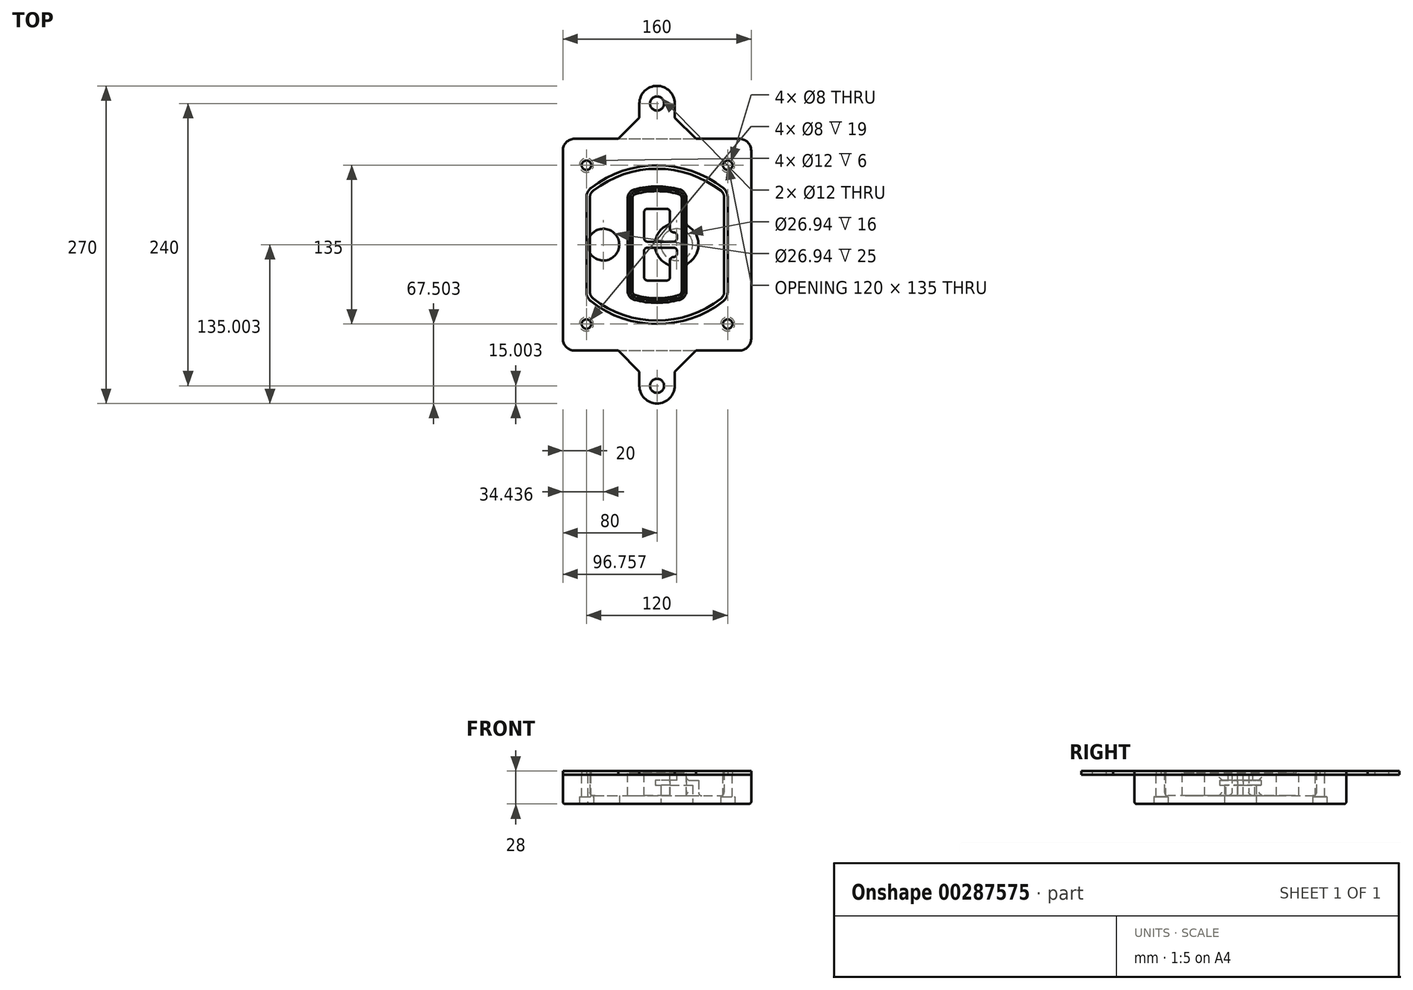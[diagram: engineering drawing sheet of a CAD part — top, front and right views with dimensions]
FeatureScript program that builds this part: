
annotation { "Feature Type Name" : "Feature", "Feature Type Description" : "" }
export const myFeature = defineFeature(function(context is Context, id is Id, definition is map)
    precondition{}
    {
        {
            var Q0;
            Q0=qCreatedBy(makeId("Top.planeOp"),FACE);
            var sketch = newSketch(context, id + "F0", { "sketchPlane" : qUnion([Q0])});
            skPoint(sketch, "E0.rect.middle", {"position": v(0, 0) * mm});
            skLineSegment(sketch, "E1.bottom", {"start": v(24.05, 28.38) * mm, "end": v(164.05, 28.38) * mm});
            skLineSegment(sketch, "E1.top", {"start": v(24.05, 208.38) * mm, "end": v(164.05, 208.38) * mm});
            skLineSegment(sketch, "E1.left", {"start": v(14.05, 38.38) * mm, "end": v(14.05, 198.38) * mm});
            skLineSegment(sketch, "E1.right", {"start": v(174.05, 38.38) * mm, "end": v(174.05, 198.38) * mm});
            skLineSegment(sketch, "E2", {"start": v(14.05, 208.38) * mm, "end": v(174.05, 28.38) * mm, "construction": true});
            skLineSegment(sketch, "E3", {"start": v(174.05, 208.38) * mm, "end": v(14.05, 28.38) * mm, "construction": true});
            skCircle(sketch, "E4", {"center": v(34.05, 185.88) * mm, "radius": 4 * mm});
            skCircle(sketch, "E5", {"center": v(154.05, 185.88) * mm, "radius": 4 * mm});
            skCircle(sketch, "E6", {"center": v(154.05, 50.88) * mm, "radius": 4 * mm});
            skCircle(sketch, "E7", {"center": v(34.05, 50.88) * mm, "radius": 4 * mm});
            skLineSegment(sketch, "E8", {"start": v(34.05, 185.88) * mm, "end": v(154.05, 185.88) * mm, "construction": true});
            skLineSegment(sketch, "E9", {"start": v(154.05, 185.88) * mm, "end": v(154.05, 50.88) * mm, "construction": true});
            skLineSegment(sketch, "E10", {"start": v(154.05, 50.88) * mm, "end": v(34.05, 50.88) * mm, "construction": true});
            skLineSegment(sketch, "E11", {"start": v(34.05, 50.88) * mm, "end": v(34.05, 185.88) * mm, "construction": true});
            skLineSegment(sketch, "E12", {"start": v(34.05, 158.68) * mm, "end": v(34.05, 78.09) * mm});
            skLineSegment(sketch, "E13", {"start": v(154.05, 158.68) * mm, "end": v(154.05, 78.09) * mm});
            skArc(sketch, "E14", {"start": v(150.2, 166.56) * mm, "mid": v(94.05, 185.88) * mm, "end": v(37.9, 166.56) * mm});
            skArc(sketch, "E15", {"start": v(37.9, 70.2) * mm, "mid": v(94.05, 50.88) * mm, "end": v(150.2, 70.2) * mm});
            skLineSegment(sketch, "E16", {"start": v(34.05, 118.38) * mm, "end": v(154.05, 118.38) * mm, "construction": true});
            skPoint(sketch, "E17.visualSharp", {"position": v(34.05, 73.38) * mm});
            skArc(sketch, "E17.filletArc", {"start": v(34.05, 78.09) * mm, "mid": v(35.06, 73.7) * mm, "end": v(37.9, 70.2) * mm});
            skPoint(sketch, "E18.visualSharp", {"position": v(34.05, 163.38) * mm});
            skArc(sketch, "E18.filletArc", {"start": v(37.9, 166.56) * mm, "mid": v(35.06, 163.06) * mm, "end": v(34.05, 158.68) * mm});
            skPoint(sketch, "E19.visualSharp", {"position": v(154.05, 163.38) * mm});
            skArc(sketch, "E19.filletArc", {"start": v(154.05, 158.68) * mm, "mid": v(153.04, 163.06) * mm, "end": v(150.2, 166.56) * mm});
            skPoint(sketch, "E20.visualSharp", {"position": v(154.05, 73.38) * mm});
            skArc(sketch, "E20.filletArc", {"start": v(150.2, 70.2) * mm, "mid": v(153.04, 73.7) * mm, "end": v(154.05, 78.09) * mm});
            skPoint(sketch, "E21.visualSharp", {"position": v(14.05, 208.38) * mm});
            skArc(sketch, "E21.filletArc", {"start": v(24.05, 208.38) * mm, "mid": v(16.98, 205.45) * mm, "end": v(14.05, 198.38) * mm});
            skPoint(sketch, "E22.visualSharp", {"position": v(174.05, 208.38) * mm});
            skArc(sketch, "E22.filletArc", {"start": v(174.05, 198.38) * mm, "mid": v(171.12, 205.45) * mm, "end": v(164.05, 208.38) * mm});
            skPoint(sketch, "E23.visualSharp", {"position": v(174.05, 28.38) * mm});
            skArc(sketch, "E23.filletArc", {"start": v(164.05, 28.38) * mm, "mid": v(171.12, 31.31) * mm, "end": v(174.05, 38.38) * mm});
            skPoint(sketch, "E24.visualSharp", {"position": v(14.05, 28.38) * mm});
            skArc(sketch, "E24.filletArc", {"start": v(14.05, 38.38) * mm, "mid": v(16.98, 31.31) * mm, "end": v(24.05, 28.38) * mm});
            skArc(sketch, "E25.0", {"start": v(151.05, 158.68) * mm, "mid": v(150.34, 161.75) * mm, "end": v(148.36, 164.2) * mm});
            skLineSegment(sketch, "E25.1", {"start": v(151.05, 158.68) * mm, "end": v(151.05, 78.09) * mm});
            skArc(sketch, "E25.2", {"start": v(148.36, 72.57) * mm, "mid": v(150.34, 75.02) * mm, "end": v(151.05, 78.09) * mm});
            skArc(sketch, "E25.3", {"start": v(39.74, 72.57) * mm, "mid": v(94.05, 53.88) * mm, "end": v(148.36, 72.57) * mm});
            skArc(sketch, "E25.4", {"start": v(37.05, 78.09) * mm, "mid": v(37.76, 75.02) * mm, "end": v(39.74, 72.57) * mm});
            skArc(sketch, "E25.5", {"start": v(148.36, 164.2) * mm, "mid": v(94.05, 182.88) * mm, "end": v(39.74, 164.2) * mm});
            skLineSegment(sketch, "E25.6", {"start": v(37.05, 158.68) * mm, "end": v(37.05, 78.09) * mm});
            skArc(sketch, "E25.7", {"start": v(39.74, 164.2) * mm, "mid": v(37.76, 161.75) * mm, "end": v(37.05, 158.68) * mm});
            skArc(sketch, "E26.0", {"start": v(35.43, 169.71) * mm, "mid": v(31.47, 164.82) * mm, "end": v(30.05, 158.68) * mm});
            skArc(sketch, "E26.1", {"start": v(152.67, 169.71) * mm, "mid": v(94.05, 189.88) * mm, "end": v(35.43, 169.71) * mm});
            skArc(sketch, "E26.2", {"start": v(158.05, 158.68) * mm, "mid": v(156.63, 164.82) * mm, "end": v(152.67, 169.71) * mm});
            skLineSegment(sketch, "E26.3", {"start": v(158.05, 158.68) * mm, "end": v(158.05, 78.09) * mm});
            skArc(sketch, "E26.4", {"start": v(152.67, 67.05) * mm, "mid": v(156.63, 71.95) * mm, "end": v(158.05, 78.09) * mm});
            skLineSegment(sketch, "E26.5", {"start": v(30.05, 158.68) * mm, "end": v(30.05, 78.09) * mm});
            skArc(sketch, "E26.6", {"start": v(35.43, 67.05) * mm, "mid": v(94.05, 46.88) * mm, "end": v(152.67, 67.05) * mm});
            skArc(sketch, "E26.7", {"start": v(30.05, 78.09) * mm, "mid": v(31.47, 71.95) * mm, "end": v(35.43, 67.05) * mm});
            skSolve(sketch);
        }
        {
            var Q0;
            Q0=makeQuery(id+"F0.imprint","IMPRINT",FACE,{"disambiguationData":[TD([[makeQuery(id+"F0.imprint","IMPRINT",EDGE,{"derivedFrom":sQuery(id+"F0.wireOp",EDGE,"E1.bottom")}),1.0]])]});
            var Q1;
            Q1=makeQuery(id+"F0.imprint","IMPRINT",FACE,{"disambiguationData":[TD([[makeQuery(id+"F0.imprint","IMPRINT",EDGE,{"derivedFrom":sQuery(id+"F0.wireOp",EDGE,"E12")}),1.0]])]});
            var Q2;
            Q2=makeQuery(id+"F0.imprint","IMPRINT",FACE,{"disambiguationData":[TD([[makeQuery(id+"F0.imprint","IMPRINT",EDGE,{"derivedFrom":sQuery(id+"F0.wireOp",EDGE,"E25.0")}),1.0]])]});
            var Q3;
            Q3=makeQuery(id+"F0.imprint","IMPRINT",FACE,{"disambiguationData":[TD([[makeQuery(id+"F0.imprint","IMPRINT",EDGE,{"derivedFrom":sQuery(id+"F0.wireOp",EDGE,"E12")}),-1.0]])]});
            extrude(context, id + "F1", {"entities" : qUnion([Q0, Q1, Q2, Q3]), "oppositeDirection" : true, "depth" : 25 * mm});
        }
        {
            var Q0;
            Q0=makeQuery(id+"F0.imprint","IMPRINT",FACE,{"disambiguationData":[TD([[makeQuery(id+"F0.imprint","IMPRINT",EDGE,{"derivedFrom":sQuery(id+"F0.wireOp",EDGE,"E12")}),1.0]])]});
            extrude(context, id + "F2", {"entities" : qUnion([Q0]), "operationType" : NewBodyOperationType.ADD, "depth" : 3 * mm});
        }
        {
            var Q0;
            Q0=makeQuery(id+"F0.imprint","IMPRINT",FACE,{"disambiguationData":[TD([[makeQuery(id+"F0.imprint","IMPRINT",EDGE,{"derivedFrom":sQuery(id+"F0.wireOp",EDGE,"E25.0")}),1.0]])]});
            extrude(context, id + "F3", {"entities" : qUnion([Q0]), "operationType" : NewBodyOperationType.REMOVE, "oppositeDirection" : true, "depth" : 18 * mm});
        }
        {
            var Q0;
            Q0=makeQuery(id+"F2.opExtrude","CAP_FACE",FACE,{"disambiguationData":[OSD([sQuery(id+"F0.wireOp",EDGE,"E12"),sQuery(id+"F0.wireOp",EDGE,"E13"),sQuery(id+"F0.wireOp",EDGE,"E14"),sQuery(id+"F0.wireOp",EDGE,"E15"),sQuery(id+"F0.wireOp",EDGE,"E17.filletArc"),sQuery(id+"F0.wireOp",EDGE,"E18.filletArc"),sQuery(id+"F0.wireOp",EDGE,"E19.filletArc"),sQuery(id+"F0.wireOp",EDGE,"E20.filletArc"),sQuery(id+"F0.wireOp",EDGE,"E25.0"),sQuery(id+"F0.wireOp",EDGE,"E25.1"),sQuery(id+"F0.wireOp",EDGE,"E25.2"),sQuery(id+"F0.wireOp",EDGE,"E25.3"),sQuery(id+"F0.wireOp",EDGE,"E25.4"),sQuery(id+"F0.wireOp",EDGE,"E25.5"),sQuery(id+"F0.wireOp",EDGE,"E25.6"),sQuery(id+"F0.wireOp",EDGE,"E25.7")])],"isStart":false});
            var sketch = newSketch(context, id + "F4", { "sketchPlane" : qUnion([Q0])});
            skArc(sketch, "E27.0", {"start": v(74.97, 71.41) * mm, "mid": v(94.05, 68.88) * mm, "end": v(113.13, 71.41) * mm});
            skArc(sketch, "E28.0", {"start": v(113.13, 165.35) * mm, "mid": v(94.05, 167.88) * mm, "end": v(74.97, 165.35) * mm});
            skLineSegment(sketch, "E29", {"start": v(69.05, 157.63) * mm, "end": v(69.05, 79.14) * mm});
            skLineSegment(sketch, "E30", {"start": v(119.05, 157.63) * mm, "end": v(119.05, 79.14) * mm});
            skLineSegment(sketch, "E31", {"start": v(69.05, 163.48) * mm, "end": v(119.05, 163.48) * mm, "construction": true});
            skLineSegment(sketch, "E32", {"start": v(69.05, 73.28) * mm, "end": v(119.05, 73.28) * mm, "construction": true});
            skPoint(sketch, "E33.visualSharp", {"position": v(69.05, 163.48) * mm});
            skArc(sketch, "E33.filletArc", {"start": v(74.97, 165.35) * mm, "mid": v(70.7, 162.5) * mm, "end": v(69.05, 157.63) * mm});
            skPoint(sketch, "E34.visualSharp", {"position": v(119.05, 163.48) * mm});
            skArc(sketch, "E34.filletArc", {"start": v(119.05, 157.63) * mm, "mid": v(117.4, 162.5) * mm, "end": v(113.13, 165.35) * mm});
            skPoint(sketch, "E35.visualSharp", {"position": v(119.05, 73.28) * mm});
            skArc(sketch, "E35.filletArc", {"start": v(113.13, 71.41) * mm, "mid": v(117.4, 74.27) * mm, "end": v(119.05, 79.14) * mm});
            skPoint(sketch, "E36.visualSharp", {"position": v(69.05, 73.28) * mm});
            skArc(sketch, "E36.filletArc", {"start": v(69.05, 79.14) * mm, "mid": v(70.7, 74.27) * mm, "end": v(74.97, 71.41) * mm});
            skArc(sketch, "E37.0", {"start": v(148.36, 164.2) * mm, "mid": v(94.05, 182.88) * mm, "end": v(39.74, 164.2) * mm});
            skArc(sketch, "E37.1", {"start": v(39.74, 164.2) * mm, "mid": v(37.76, 161.75) * mm, "end": v(37.05, 158.68) * mm});
            skLineSegment(sketch, "E37.2", {"start": v(37.05, 158.68) * mm, "end": v(37.05, 78.09) * mm});
            skArc(sketch, "E37.3", {"start": v(37.05, 78.09) * mm, "mid": v(37.76, 75.02) * mm, "end": v(39.74, 72.57) * mm});
            skArc(sketch, "E37.4", {"start": v(39.74, 72.57) * mm, "mid": v(94.05, 53.88) * mm, "end": v(148.36, 72.57) * mm});
            skArc(sketch, "E37.5", {"start": v(148.36, 72.57) * mm, "mid": v(150.34, 75.02) * mm, "end": v(151.05, 78.09) * mm});
            skLineSegment(sketch, "E37.6", {"start": v(151.05, 158.68) * mm, "end": v(151.05, 78.09) * mm});
            skArc(sketch, "E37.7", {"start": v(151.05, 158.68) * mm, "mid": v(150.34, 161.75) * mm, "end": v(148.36, 164.2) * mm});
            skLineSegment(sketch, "E38.0", {"start": v(117.05, 157.63) * mm, "end": v(117.05, 79.14) * mm});
            skArc(sketch, "E38.1", {"start": v(112.61, 73.34) * mm, "mid": v(115.81, 75.49) * mm, "end": v(117.05, 79.14) * mm});
            skArc(sketch, "E38.2", {"start": v(75.49, 73.34) * mm, "mid": v(94.05, 70.88) * mm, "end": v(112.61, 73.34) * mm});
            skArc(sketch, "E38.3", {"start": v(71.05, 79.14) * mm, "mid": v(72.29, 75.49) * mm, "end": v(75.49, 73.34) * mm});
            skLineSegment(sketch, "E38.4", {"start": v(71.05, 157.63) * mm, "end": v(71.05, 79.14) * mm});
            skArc(sketch, "E38.5", {"start": v(117.05, 157.63) * mm, "mid": v(115.81, 161.28) * mm, "end": v(112.61, 163.42) * mm});
            skArc(sketch, "E38.6", {"start": v(75.49, 163.42) * mm, "mid": v(72.29, 161.28) * mm, "end": v(71.05, 157.63) * mm});
            skArc(sketch, "E38.7", {"start": v(112.61, 163.42) * mm, "mid": v(94.05, 165.88) * mm, "end": v(75.49, 163.42) * mm});
            skArc(sketch, "E39.0", {"start": v(115.05, 157.63) * mm, "mid": v(114.23, 160.06) * mm, "end": v(112.1, 161.5) * mm});
            skLineSegment(sketch, "E39.1", {"start": v(115.05, 157.63) * mm, "end": v(115.05, 79.14) * mm});
            skArc(sketch, "E39.2", {"start": v(112.1, 75.27) * mm, "mid": v(114.23, 76.7) * mm, "end": v(115.05, 79.14) * mm});
            skArc(sketch, "E39.3", {"start": v(76, 75.27) * mm, "mid": v(94.05, 72.88) * mm, "end": v(112.1, 75.27) * mm});
            skArc(sketch, "E39.4", {"start": v(73.05, 79.14) * mm, "mid": v(73.87, 76.7) * mm, "end": v(76, 75.27) * mm});
            skArc(sketch, "E39.5", {"start": v(112.1, 161.5) * mm, "mid": v(94.05, 163.88) * mm, "end": v(76, 161.5) * mm});
            skLineSegment(sketch, "E39.6", {"start": v(73.05, 157.63) * mm, "end": v(73.05, 79.14) * mm});
            skArc(sketch, "E39.7", {"start": v(76, 161.5) * mm, "mid": v(73.87, 160.06) * mm, "end": v(73.05, 157.63) * mm});
            skLineSegment(sketch, "E40", {"start": v(69.05, 118.38) * mm, "end": v(119.05, 118.38) * mm, "construction": true});
            skLineSegment(sketch, "E41", {"start": v(83.05, 123.88) * mm, "end": v(83.05, 145.88) * mm});
            skLineSegment(sketch, "E42", {"start": v(86.05, 148.88) * mm, "end": v(102.05, 148.88) * mm});
            skLineSegment(sketch, "E43", {"start": v(105.05, 145.88) * mm, "end": v(105.05, 131.88) * mm});
            skLineSegment(sketch, "E44", {"start": v(108.05, 128.88) * mm, "end": v(108.05, 128.88) * mm});
            skLineSegment(sketch, "E45", {"start": v(111.05, 125.88) * mm, "end": v(111.05, 123.88) * mm});
            skLineSegment(sketch, "E46", {"start": v(108.05, 120.88) * mm, "end": v(86.05, 120.88) * mm});
            skPoint(sketch, "E47.visualSharp", {"position": v(83.05, 148.88) * mm});
            skArc(sketch, "E47.filletArc", {"start": v(86.05, 148.88) * mm, "mid": v(83.93, 148) * mm, "end": v(83.05, 145.88) * mm});
            skPoint(sketch, "E48.visualSharp", {"position": v(105.05, 148.88) * mm});
            skArc(sketch, "E48.filletArc", {"start": v(105.05, 145.88) * mm, "mid": v(104.17, 148) * mm, "end": v(102.05, 148.88) * mm});
            skPoint(sketch, "E49.visualSharp", {"position": v(105.05, 128.88) * mm});
            skArc(sketch, "E49.filletArc", {"start": v(105.05, 131.88) * mm, "mid": v(105.93, 129.76) * mm, "end": v(108.05, 128.88) * mm});
            skPoint(sketch, "E50.visualSharp", {"position": v(111.05, 128.88) * mm});
            skArc(sketch, "E50.filletArc", {"start": v(111.05, 125.88) * mm, "mid": v(110.17, 128) * mm, "end": v(108.05, 128.88) * mm});
            skPoint(sketch, "E51.visualSharp", {"position": v(111.05, 120.88) * mm});
            skArc(sketch, "E51.filletArc", {"start": v(108.05, 120.88) * mm, "mid": v(110.17, 121.76) * mm, "end": v(111.05, 123.88) * mm});
            skPoint(sketch, "E52.visualSharp", {"position": v(83.05, 120.88) * mm});
            skArc(sketch, "E52.filletArc", {"start": v(83.05, 123.88) * mm, "mid": v(83.93, 121.76) * mm, "end": v(86.05, 120.88) * mm});
            skLineSegment(sketch, "E53.0.MirrorCS", {"start": v(108.05, 115.88) * mm, "end": v(86.05, 115.88) * mm});
            skArc(sketch, "E54.0.MirrorCS", {"start": v(83.05, 112.88) * mm, "mid": v(83.93, 115) * mm, "end": v(86.05, 115.88) * mm});
            skLineSegment(sketch, "E55.0.MirrorCS", {"start": v(83.05, 112.88) * mm, "end": v(83.05, 90.88) * mm});
            skArc(sketch, "E56.0.MirrorCS", {"start": v(86.05, 87.88) * mm, "mid": v(83.93, 88.76) * mm, "end": v(83.05, 90.88) * mm});
            skLineSegment(sketch, "E57.0.MirrorCS", {"start": v(86.05, 87.88) * mm, "end": v(102.05, 87.88) * mm});
            skArc(sketch, "E58.0.MirrorCS", {"start": v(105.05, 90.88) * mm, "mid": v(104.17, 88.76) * mm, "end": v(102.05, 87.88) * mm});
            skLineSegment(sketch, "E59.0.MirrorCS", {"start": v(105.05, 90.88) * mm, "end": v(105.05, 104.88) * mm});
            skArc(sketch, "E60.0.MirrorCS", {"start": v(105.05, 104.88) * mm, "mid": v(105.93, 107) * mm, "end": v(108.05, 107.88) * mm});
            skArc(sketch, "E61.0.MirrorCS", {"start": v(111.05, 110.88) * mm, "mid": v(110.17, 108.76) * mm, "end": v(108.05, 107.88) * mm});
            skLineSegment(sketch, "E62.0.MirrorCS", {"start": v(111.05, 110.88) * mm, "end": v(111.05, 112.88) * mm});
            skArc(sketch, "E63.0.MirrorCS", {"start": v(108.05, 115.88) * mm, "mid": v(110.17, 115) * mm, "end": v(111.05, 112.88) * mm});
            skSolve(sketch);
        }
        {
            var Q0;
            Q0=makeQuery(id+"F4.imprint","IMPRINT",FACE,{"disambiguationData":[TD([[makeQuery(id+"F4.imprint","IMPRINT",EDGE,{"derivedFrom":sQuery(id+"F4.wireOp",EDGE,"E27.0")}),1.0]])]});
            var Q1;
            Q1=makeQuery(id+"F4.imprint","IMPRINT",FACE,{"disambiguationData":[TD([[makeQuery(id+"F4.imprint","IMPRINT",EDGE,{"derivedFrom":sQuery(id+"F4.wireOp",EDGE,"E38.0")}),-1.0]])]});
            var Q2;
            Q2=makeQuery(id+"F4.imprint","IMPRINT",FACE,{"disambiguationData":[TD([[makeQuery(id+"F4.imprint","IMPRINT",EDGE,{"derivedFrom":sQuery(id+"F4.wireOp",EDGE,"E39.0")}),1.0]])]});
            extrude(context, id + "F5", {"entities" : qUnion([Q0, Q1, Q2]), "operationType" : NewBodyOperationType.ADD, "endBound" : BoundingType.UP_TO_NEXT, "oppositeDirection" : true, "depth" : 25 * mm});
        }
        {
            var Q0;
            Q0=makeQuery(id+"F4.imprint","IMPRINT",FACE,{"disambiguationData":[TD([[makeQuery(id+"F4.imprint","IMPRINT",EDGE,{"derivedFrom":sQuery(id+"F4.wireOp",EDGE,"E38.0")}),-1.0]])]});
            extrude(context, id + "F6", {"entities" : qUnion([Q0]), "operationType" : NewBodyOperationType.REMOVE, "oppositeDirection" : true, "depth" : 2 * mm});
        }
        {
            var Q0;
            Q0=makeQuery(id+"F1.opExtrude","CAP_FACE",FACE,{"disambiguationData":[OSD([sQuery(id+"F0.wireOp",EDGE,"E1.bottom"),sQuery(id+"F0.wireOp",EDGE,"E1.top"),sQuery(id+"F0.wireOp",EDGE,"E1.left"),sQuery(id+"F0.wireOp",EDGE,"E1.right"),sQuery(id+"F0.wireOp",EDGE,"E4"),sQuery(id+"F0.wireOp",EDGE,"E5"),sQuery(id+"F0.wireOp",EDGE,"E6"),sQuery(id+"F0.wireOp",EDGE,"E7"),sQuery(id+"F0.wireOp",EDGE,"E21.filletArc"),sQuery(id+"F0.wireOp",EDGE,"E22.filletArc"),sQuery(id+"F0.wireOp",EDGE,"E23.filletArc"),sQuery(id+"F0.wireOp",EDGE,"E24.filletArc")])],"isStart":false});
            var sketch = newSketch(context, id + "F7", { "sketchPlane" : qUnion([Q0])});
            skCircle(sketch, "E64", {"center": v(110.8, -118.38) * mm, "radius": 13.47 * mm});
            skCircle(sketch, "E65", {"center": v(48.49, -118.38) * mm, "radius": 13.47 * mm});
            skLineSegment(sketch, "E66", {"start": v(174.05, -118.38) * mm, "end": v(14.05, -118.38) * mm});
            skCircle(sketch, "E67", {"center": v(110.8, -118.38) * mm, "radius": 18.47 * mm});
            skCircle(sketch, "E68", {"center": v(154.05, -185.88) * mm, "radius": 6 * mm});
            skCircle(sketch, "E69", {"center": v(34.05, -185.88) * mm, "radius": 6 * mm});
            skCircle(sketch, "E70", {"center": v(34.05, -50.88) * mm, "radius": 6 * mm});
            skCircle(sketch, "E71", {"center": v(154.05, -50.88) * mm, "radius": 6 * mm});
            skSolve(sketch);
        }
        {
            var Q0;
            {var subQ1=sQuery(id+"F7.wireOp",EDGE,"E66");var subQ4=sQuery(id+"F7.wireOp",EDGE,"E64");var subQ6=makeQuery(id+"F7.imprint","INTERSECT",VERTEX,{"disambiguationData":[OD(0.0)],"derivedFrom":[subQ4,subQ1]});Q0=makeQuery(id+"F7.imprint","IMPRINT",FACE,{"disambiguationData":[TD([[makeQuery(id+"F7.imprint","IMPRINT",EDGE,{"disambiguationData":[TD([[subQ6,-1.0]])],"derivedFrom":subQ4}),-1.0]])]});}
            var Q1;
            {var subQ0=sQuery(id+"F7.wireOp",EDGE,"E66");var subQ1=sQuery(id+"F7.wireOp",EDGE,"E64");var subQ3=makeQuery(id+"F7.imprint","INTERSECT",VERTEX,{"disambiguationData":[OD(0.0)],"derivedFrom":[subQ1,subQ0]});Q1=makeQuery(id+"F7.imprint","IMPRINT",FACE,{"disambiguationData":[TD([[makeQuery(id+"F7.imprint","IMPRINT",EDGE,{"disambiguationData":[TD([[subQ3,-1.0]])],"derivedFrom":subQ1}),1.0]])]});}
            var Q2;
            {var subQ0=sQuery(id+"F7.wireOp",EDGE,"E66");var subQ1=sQuery(id+"F7.wireOp",EDGE,"E64");var subQ3=makeQuery(id+"F7.imprint","INTERSECT",VERTEX,{"disambiguationData":[OD(0.0)],"derivedFrom":[subQ1,subQ0]});Q2=makeQuery(id+"F7.imprint","IMPRINT",FACE,{"disambiguationData":[TD([[makeQuery(id+"F7.imprint","IMPRINT",EDGE,{"disambiguationData":[TD([[subQ3,1.0]])],"derivedFrom":subQ1}),1.0]])]});}
            var Q3;
            {var subQ1=sQuery(id+"F7.wireOp",EDGE,"E66");var subQ4=sQuery(id+"F7.wireOp",EDGE,"E64");var subQ6=makeQuery(id+"F7.imprint","INTERSECT",VERTEX,{"disambiguationData":[OD(0.0)],"derivedFrom":[subQ4,subQ1]});Q3=makeQuery(id+"F7.imprint","IMPRINT",FACE,{"disambiguationData":[TD([[makeQuery(id+"F7.imprint","IMPRINT",EDGE,{"disambiguationData":[TD([[subQ6,1.0]])],"derivedFrom":subQ4}),-1.0]])]});}
            extrude(context, id + "F8", {"entities" : qUnion([Q0, Q1, Q2, Q3]), "operationType" : NewBodyOperationType.ADD, "oppositeDirection" : true, "depth" : 20 * mm});
        }
        {
            var Q0;
            {var subQ0=sQuery(id+"F7.wireOp",EDGE,"E66");var subQ1=sQuery(id+"F7.wireOp",EDGE,"E64");var subQ3=makeQuery(id+"F7.imprint","INTERSECT",VERTEX,{"disambiguationData":[OD(0.0)],"derivedFrom":[subQ1,subQ0]});Q0=makeQuery(id+"F7.imprint","IMPRINT",FACE,{"disambiguationData":[TD([[makeQuery(id+"F7.imprint","IMPRINT",EDGE,{"disambiguationData":[TD([[subQ3,-1.0]])],"derivedFrom":subQ1}),1.0]])]});}
            var Q1;
            {var subQ0=sQuery(id+"F7.wireOp",EDGE,"E66");var subQ1=sQuery(id+"F7.wireOp",EDGE,"E64");var subQ3=makeQuery(id+"F7.imprint","INTERSECT",VERTEX,{"disambiguationData":[OD(0.0)],"derivedFrom":[subQ1,subQ0]});Q1=makeQuery(id+"F7.imprint","IMPRINT",FACE,{"disambiguationData":[TD([[makeQuery(id+"F7.imprint","IMPRINT",EDGE,{"disambiguationData":[TD([[subQ3,1.0]])],"derivedFrom":subQ1}),1.0]])]});}
            extrude(context, id + "F9", {"entities" : qUnion([Q0, Q1]), "operationType" : NewBodyOperationType.REMOVE, "oppositeDirection" : true, "depth" : 16 * mm});
        }
        {
            var Q0;
            {var subQ0=sQuery(id+"F7.wireOp",EDGE,"E66");var subQ1=sQuery(id+"F7.wireOp",EDGE,"E65");var subQ3=makeQuery(id+"F7.imprint","INTERSECT",VERTEX,{"disambiguationData":[OD(0.0)],"derivedFrom":[subQ1,subQ0]});Q0=makeQuery(id+"F7.imprint","IMPRINT",FACE,{"disambiguationData":[TD([[makeQuery(id+"F7.imprint","IMPRINT",EDGE,{"disambiguationData":[TD([[subQ3,-1.0]])],"derivedFrom":subQ1}),1.0]])]});}
            var Q1;
            {var subQ0=sQuery(id+"F7.wireOp",EDGE,"E66");var subQ1=sQuery(id+"F7.wireOp",EDGE,"E65");var subQ3=makeQuery(id+"F7.imprint","INTERSECT",VERTEX,{"disambiguationData":[OD(0.0)],"derivedFrom":[subQ1,subQ0]});Q1=makeQuery(id+"F7.imprint","IMPRINT",FACE,{"disambiguationData":[TD([[makeQuery(id+"F7.imprint","IMPRINT",EDGE,{"disambiguationData":[TD([[subQ3,1.0]])],"derivedFrom":subQ1}),1.0]])]});}
            extrude(context, id + "F10", {"entities" : qUnion([Q0, Q1]), "operationType" : NewBodyOperationType.REMOVE, "oppositeDirection" : true, "depth" : 25 * mm});
        }
        {
            var Q0;
            Q0=makeQuery(id+"F7.imprint","IMPRINT",FACE,{"disambiguationData":[TD([[makeQuery(id+"F7.imprint","IMPRINT",EDGE,{"derivedFrom":sQuery(id+"F7.wireOp",EDGE,"E68")}),1.0]])]});
            var Q1;
            Q1=makeQuery(id+"F7.imprint","IMPRINT",FACE,{"disambiguationData":[TD([[makeQuery(id+"F7.imprint","IMPRINT",EDGE,{"derivedFrom":makeQuery(id+"F1.opExtrude","CAP_EDGE",EDGE,{"disambiguationData":[OSD([sQuery(id+"F0.wireOp",EDGE,"E5")])],"isStart":false})}),-1.0]])]});
            var Q2;
            Q2=makeQuery(id+"F7.imprint","IMPRINT",FACE,{"disambiguationData":[TD([[makeQuery(id+"F7.imprint","IMPRINT",EDGE,{"derivedFrom":sQuery(id+"F7.wireOp",EDGE,"E69")}),1.0]])]});
            var Q3;
            Q3=makeQuery(id+"F7.imprint","IMPRINT",FACE,{"disambiguationData":[TD([[makeQuery(id+"F7.imprint","IMPRINT",EDGE,{"derivedFrom":makeQuery(id+"F1.opExtrude","CAP_EDGE",EDGE,{"disambiguationData":[OSD([sQuery(id+"F0.wireOp",EDGE,"E4")])],"isStart":false})}),-1.0]])]});
            var Q4;
            Q4=makeQuery(id+"F7.imprint","IMPRINT",FACE,{"disambiguationData":[TD([[makeQuery(id+"F7.imprint","IMPRINT",EDGE,{"derivedFrom":sQuery(id+"F7.wireOp",EDGE,"E70")}),1.0]])]});
            var Q5;
            Q5=makeQuery(id+"F7.imprint","IMPRINT",FACE,{"disambiguationData":[TD([[makeQuery(id+"F7.imprint","IMPRINT",EDGE,{"derivedFrom":makeQuery(id+"F1.opExtrude","CAP_EDGE",EDGE,{"disambiguationData":[OSD([sQuery(id+"F0.wireOp",EDGE,"E7")])],"isStart":false})}),-1.0]])]});
            var Q6;
            Q6=makeQuery(id+"F7.imprint","IMPRINT",FACE,{"disambiguationData":[TD([[makeQuery(id+"F7.imprint","IMPRINT",EDGE,{"derivedFrom":sQuery(id+"F7.wireOp",EDGE,"E71")}),1.0]])]});
            var Q7;
            Q7=makeQuery(id+"F7.imprint","IMPRINT",FACE,{"disambiguationData":[TD([[makeQuery(id+"F7.imprint","IMPRINT",EDGE,{"derivedFrom":makeQuery(id+"F1.opExtrude","CAP_EDGE",EDGE,{"disambiguationData":[OSD([sQuery(id+"F0.wireOp",EDGE,"E6")])],"isStart":false})}),-1.0]])]});
            extrude(context, id + "F11", {"entities" : qUnion([Q0, Q1, Q2, Q3, Q4, Q5, Q6, Q7]), "operationType" : NewBodyOperationType.REMOVE, "oppositeDirection" : true, "depth" : 6 * mm});
        }
        {
            var Q0;
            Q0=makeQuery(id+"F9.boolean.opBoolean","COPY",FACE,{"derivedFrom":makeQuery(id+"F9.opExtrude","CAP_FACE",FACE,{"disambiguationData":[OSD([sQuery(id+"F7.wireOp",EDGE,"E64")])],"isStart":false})});
            var sketch = newSketch(context, id + "F12", { "sketchPlane" : qUnion([Q0])});
            skArc(sketch, "E72.0", {"start": v(105.05, -100.83) * mm, "mid": v(96.62, -106.56) * mm, "end": v(92.5, -115.88) * mm});
            skArc(sketch, "E72.1", {"start": v(92.5, -120.88) * mm, "mid": v(96.62, -130.2) * mm, "end": v(105.05, -135.93) * mm});
            skLineSegment(sketch, "E73", {"start": v(92.5, -120.88) * mm, "end": v(108.05, -120.88) * mm});
            skLineSegment(sketch, "E74.0", {"start": v(108.05, -115.88) * mm, "end": v(92.5, -115.88) * mm});
            skArc(sketch, "E74.1", {"start": v(108.05, -115.88) * mm, "mid": v(110.17, -115) * mm, "end": v(111.05, -112.88) * mm});
            skLineSegment(sketch, "E74.2", {"start": v(111.05, -110.88) * mm, "end": v(111.05, -112.88) * mm});
            skArc(sketch, "E74.3", {"start": v(111.05, -110.88) * mm, "mid": v(110.17, -108.76) * mm, "end": v(108.05, -107.88) * mm});
            skArc(sketch, "E74.4", {"start": v(105.05, -104.88) * mm, "mid": v(105.93, -107) * mm, "end": v(108.05, -107.88) * mm});
            skLineSegment(sketch, "E74.5", {"start": v(105.05, -100.83) * mm, "end": v(105.05, -104.88) * mm});
            skLineSegment(sketch, "E74.7", {"start": v(108.05, -120.88) * mm, "end": v(92.5, -120.88) * mm});
            skArc(sketch, "E74.8", {"start": v(108.05, -120.88) * mm, "mid": v(110.17, -121.76) * mm, "end": v(111.05, -123.88) * mm});
            skLineSegment(sketch, "E74.9", {"start": v(111.05, -125.88) * mm, "end": v(111.05, -123.88) * mm});
            skArc(sketch, "E74.10", {"start": v(111.05, -125.88) * mm, "mid": v(110.17, -128) * mm, "end": v(108.05, -128.88) * mm});
            skArc(sketch, "E74.11", {"start": v(105.05, -131.88) * mm, "mid": v(105.93, -129.76) * mm, "end": v(108.05, -128.88) * mm});
            skLineSegment(sketch, "E74.12", {"start": v(105.05, -135.93) * mm, "end": v(105.05, -131.88) * mm});
            skPoint(sketch, "E75.orphan", {"position": v(105.05, -145.88) * mm});
            skPoint(sketch, "E76.orphan", {"position": v(86.05, -120.88) * mm});
            skPoint(sketch, "E77.orphan", {"position": v(86.05, -115.88) * mm});
            skPoint(sketch, "E78.orphan", {"position": v(105.05, -90.88) * mm});
            skSolve(sketch);
        }
        {
            var Q0;
            {var subQ7=sQuery(id+"F12.wireOp",EDGE,"E72.0");var subQ14=sQuery(id+"F12.wireOp",EDGE,"E72.1");var subQ16=sQuery(id+"F12.wireOp",EDGE,"E74.1");var subQ18=sQuery(id+"F12.wireOp",EDGE,"E74.8");Q0=qUnion([makeQuery(id+"F12.imprint","IMPRINT",FACE,{"disambiguationData":[TD([[makeQuery(id+"F12.imprint","IMPRINT",EDGE,{"derivedFrom":subQ7}),1.0]])]}),makeQuery(id+"F12.imprint","IMPRINT",FACE,{"disambiguationData":[TD([[makeQuery(id+"F12.imprint","IMPRINT",EDGE,{"derivedFrom":subQ14}),1.0]])]}),makeQuery(id+"F12.imprint","IMPRINT",FACE,{"disambiguationData":[TD([[makeQuery(id+"F12.imprint","IMPRINT",EDGE,{"derivedFrom":subQ16}),1.0]])]}),makeQuery(id+"F12.imprint","IMPRINT",FACE,{"disambiguationData":[TD([[makeQuery(id+"F12.imprint","IMPRINT",EDGE,{"derivedFrom":subQ18}),-1.0]])]})]);}
            var Q1;
            Q1=makeQuery(id+"F5.boolean.opBoolean","SPLIT",FACE,{"disambiguationData":[TD([makeQuery(id+"F5.opExtrude","SWEPT_FACE",FACE,{"disambiguationData":[OSD([sQuery(id+"F4.wireOp",EDGE,"E41")])]})])],"derivedFrom":makeQuery(id+"F3.boolean.opBoolean","COPY",FACE,{"derivedFrom":makeQuery(id+"F3.opExtrude","CAP_FACE",FACE,{"disambiguationData":[OSD([sQuery(id+"F0.wireOp",EDGE,"E25.0"),sQuery(id+"F0.wireOp",EDGE,"E25.1"),sQuery(id+"F0.wireOp",EDGE,"E25.2"),sQuery(id+"F0.wireOp",EDGE,"E25.3"),sQuery(id+"F0.wireOp",EDGE,"E25.4"),sQuery(id+"F0.wireOp",EDGE,"E25.5"),sQuery(id+"F0.wireOp",EDGE,"E25.6"),sQuery(id+"F0.wireOp",EDGE,"E25.7")])],"isStart":false})})});
            extrude(context, id + "F13", {"entities" : qUnion([Q0]), "operationType" : NewBodyOperationType.REMOVE, "endBound" : BoundingType.UP_TO_SURFACE, "endBoundEntityFace" : qUnion([Q1]), "depth" : 25 * mm});
        }
        {
            var Q0;
            {var subQ0=sQuery(id+"F0.wireOp",EDGE,"E25.6");var subQ1=makeQuery(id+"F3.boolean.opBoolean","COPY",EDGE,{"derivedFrom":makeQuery(id+"F3.opExtrude","CAP_EDGE",EDGE,{"disambiguationData":[OSD([subQ0])],"isStart":false})});var subQ4=sQuery(id+"F0.wireOp",EDGE,"E25.4");var subQ5=sQuery(id+"F0.wireOp",EDGE,"E25.7");Q0=qUnion([makeQuery(id+"F10.boolean.opBoolean","SPLIT",EDGE,{"disambiguationData":[TD([makeQuery(id+"F2.opExtrude","SWEPT_FACE",FACE,{"disambiguationData":[OSD([subQ4])]})])],"derivedFrom":subQ1}),makeQuery(id+"F10.boolean.opBoolean","SPLIT",EDGE,{"disambiguationData":[TD([makeQuery(id+"F2.opExtrude","SWEPT_FACE",FACE,{"disambiguationData":[OSD([subQ5])]})])],"derivedFrom":subQ1})]);}
            var Q1;
            Q1=makeQuery(id+"F8.boolean.opBoolean","INTERSECT",EDGE,{"derivedFrom":[makeQuery(id+"F5.opExtrude","SWEPT_FACE",FACE,{"disambiguationData":[OSD([sQuery(id+"F4.wireOp",EDGE,"E30")])]}),makeQuery(id+"F8.opExtrude","CAP_FACE",FACE,{"disambiguationData":[OSD([sQuery(id+"F7.wireOp",EDGE,"E67")])],"isStart":false})]});
            var Q2;
            Q2=makeQuery(id+"F8.boolean.opBoolean","INTERSECT",EDGE,{"disambiguationData":[OD(1.0)],"derivedFrom":[makeQuery(id+"F5.opExtrude","SWEPT_FACE",FACE,{"disambiguationData":[OSD([sQuery(id+"F4.wireOp",EDGE,"E30")])]}),makeQuery(id+"F8.opExtrude","SWEPT_FACE",FACE,{"disambiguationData":[OSD([sQuery(id+"F7.wireOp",EDGE,"E67")])]})]});
            var Q3;
            {var subQ0=sQuery(id+"F4.wireOp",EDGE,"E30");Q3=makeQuery(id+"F8.boolean.opBoolean","SPLIT",EDGE,{"disambiguationData":[TD([makeQuery(id+"F5.opExtrude","SWEPT_FACE",FACE,{"disambiguationData":[OSD([sQuery(id+"F4.wireOp",EDGE,"E35.filletArc")])]})])],"derivedFrom":makeQuery(id+"F5.opExtrude","CAP_EDGE",EDGE,{"disambiguationData":[OSD([subQ0])],"isStart":false})});}
            var Q4;
            {var subQ0=sQuery(id+"F0.wireOp",EDGE,"E25.7");var subQ1=sQuery(id+"F0.wireOp",EDGE,"E25.1");var subQ2=sQuery(id+"F0.wireOp",EDGE,"E25.6");var subQ3=sQuery(id+"F0.wireOp",EDGE,"E25.5");var subQ4=sQuery(id+"F0.wireOp",EDGE,"E25.4");var subQ5=sQuery(id+"F0.wireOp",EDGE,"E25.0");var subQ6=sQuery(id+"F0.wireOp",EDGE,"E25.2");var subQ7=sQuery(id+"F0.wireOp",EDGE,"E25.3");Q4=makeQuery(id+"F8.boolean.opBoolean","INTERSECT",EDGE,{"derivedFrom":[makeQuery(id+"F5.boolean.opBoolean","SPLIT",FACE,{"disambiguationData":[TD([makeQuery(id+"F2.opExtrude","SWEPT_FACE",FACE,{"disambiguationData":[OSD([subQ5])]})])],"derivedFrom":makeQuery(id+"F3.boolean.opBoolean","COPY",FACE,{"derivedFrom":makeQuery(id+"F3.opExtrude","CAP_FACE",FACE,{"disambiguationData":[OSD([subQ5,subQ1,subQ6,subQ7,subQ4,subQ3,subQ2,subQ0])],"isStart":false})})}),makeQuery(id+"F8.opExtrude","SWEPT_FACE",FACE,{"disambiguationData":[OSD([sQuery(id+"F7.wireOp",EDGE,"E67")])]})]});}
            var Q5;
            Q5=makeQuery(id+"F8.boolean.opBoolean","INTERSECT",EDGE,{"disambiguationData":[OD(0.0)],"derivedFrom":[makeQuery(id+"F5.opExtrude","SWEPT_FACE",FACE,{"disambiguationData":[OSD([sQuery(id+"F4.wireOp",EDGE,"E30")])]}),makeQuery(id+"F8.opExtrude","SWEPT_FACE",FACE,{"disambiguationData":[OSD([sQuery(id+"F7.wireOp",EDGE,"E67")])]})]});
            fillet(context, id + "F14", {"entities" : qUnion([Q0, Q1, Q2, Q3, Q4, Q5]), "radius" : 3 * mm, "tangentPropagation" : true, "allowEdgeOverflow" : false});
        }
        {
            var Q0;
            Q0=makeQuery(id+"F1.opExtrude","CAP_EDGE",EDGE,{"disambiguationData":[OSD([sQuery(id+"F0.wireOp",EDGE,"E1.bottom")])],"isStart":false});
            fillet(context, id + "F15", {"entities" : qUnion([Q0]), "radius" : 2 * mm, "tangentPropagation" : true, "allowEdgeOverflow" : false});
        }
        {
            var Q0;
            {var subQ0=sQuery(id+"F0.wireOp",EDGE,"E1.bottom");var subQ1=sQuery(id+"F0.wireOp",EDGE,"E1.top");var subQ2=sQuery(id+"F0.wireOp",EDGE,"E1.left");var subQ3=sQuery(id+"F0.wireOp",EDGE,"E1.right");var subQ4=sQuery(id+"F0.wireOp",EDGE,"E4");var subQ5=sQuery(id+"F0.wireOp",EDGE,"E5");var subQ6=sQuery(id+"F0.wireOp",EDGE,"E6");var subQ7=sQuery(id+"F0.wireOp",EDGE,"E7");var subQ8=sQuery(id+"F0.wireOp",EDGE,"E21.filletArc");var subQ9=sQuery(id+"F0.wireOp",EDGE,"E22.filletArc");var subQ10=sQuery(id+"F0.wireOp",EDGE,"E23.filletArc");var subQ11=sQuery(id+"F0.wireOp",EDGE,"E24.filletArc");Q0=makeQuery(id+"F2.boolean.opBoolean","SPLIT",FACE,{"disambiguationData":[TD([makeQuery(id+"F1.opExtrude","SWEPT_FACE",FACE,{"disambiguationData":[OSD([subQ0])]})])],"derivedFrom":makeQuery(id+"F1.opExtrude","CAP_FACE",FACE,{"disambiguationData":[OSD([subQ0,subQ1,subQ2,subQ3,subQ4,subQ5,subQ6,subQ7,subQ8,subQ9,subQ10,subQ11])],"isStart":true})});}
            var sketch = newSketch(context, id + "F16", { "sketchPlane" : qUnion([Q0])});
            skLineSegment(sketch, "E79.0", {"start": v(14.05, 38.38) * mm, "end": v(14.05, 198.38) * mm});
            skArc(sketch, "E79.1", {"start": v(24.05, 208.38) * mm, "mid": v(16.98, 205.45) * mm, "end": v(14.05, 198.38) * mm});
            skLineSegment(sketch, "E79.2", {"start": v(24.05, 208.38) * mm, "end": v(164.05, 208.38) * mm});
            skArc(sketch, "E79.5", {"start": v(164.05, 28.38) * mm, "mid": v(171.12, 31.31) * mm, "end": v(174.05, 38.38) * mm});
            skLineSegment(sketch, "E79.6", {"start": v(24.05, 28.38) * mm, "end": v(164.05, 28.38) * mm});
            skArc(sketch, "E79.7", {"start": v(14.05, 38.38) * mm, "mid": v(16.98, 31.31) * mm, "end": v(24.05, 28.38) * mm});
            skCircle(sketch, "E79.8", {"center": v(34.05, 50.88) * mm, "radius": 4 * mm});
            skCircle(sketch, "E79.9", {"center": v(34.05, 185.88) * mm, "radius": 4 * mm});
            skCircle(sketch, "E79.10", {"center": v(154.05, 185.88) * mm, "radius": 4 * mm});
            skCircle(sketch, "E79.11", {"center": v(154.05, 50.88) * mm, "radius": 4 * mm});
            skArc(sketch, "E79.12", {"start": v(154.05, 158.68) * mm, "mid": v(153.04, 163.06) * mm, "end": v(150.2, 166.56) * mm});
            skLineSegment(sketch, "E79.13", {"start": v(154.05, 158.68) * mm, "end": v(154.05, 78.09) * mm});
            skArc(sketch, "E79.14", {"start": v(150.2, 70.2) * mm, "mid": v(153.04, 73.7) * mm, "end": v(154.05, 78.09) * mm});
            skArc(sketch, "E79.15", {"start": v(37.9, 70.2) * mm, "mid": v(94.05, 50.88) * mm, "end": v(150.2, 70.2) * mm});
            skArc(sketch, "E79.16", {"start": v(34.05, 78.09) * mm, "mid": v(35.06, 73.7) * mm, "end": v(37.9, 70.2) * mm});
            skLineSegment(sketch, "E79.17", {"start": v(34.05, 158.68) * mm, "end": v(34.05, 78.09) * mm});
            skArc(sketch, "E79.18", {"start": v(37.9, 166.56) * mm, "mid": v(35.06, 163.06) * mm, "end": v(34.05, 158.68) * mm});
            skArc(sketch, "E79.19", {"start": v(150.2, 166.56) * mm, "mid": v(94.05, 185.88) * mm, "end": v(37.9, 166.56) * mm});
            skLineSegment(sketch, "E80", {"start": v(94.05, 208.38) * mm, "end": v(94.05, 238.38) * mm, "construction": true});
            skLineSegment(sketch, "E81", {"start": v(61.05, 208.38) * mm, "end": v(79.05, 226.38) * mm});
            skLineSegment(sketch, "E82", {"start": v(79.05, 226.38) * mm, "end": v(79.05, 238.38) * mm});
            skArc(sketch, "E83", {"start": v(79.05, 238.38) * mm, "mid": v(94.05, 253.38) * mm, "end": v(109.05, 238.38) * mm});
            skLineSegment(sketch, "E84", {"start": v(109.05, 238.38) * mm, "end": v(109.05, 226.38) * mm});
            skLineSegment(sketch, "E85", {"start": v(109.05, 226.38) * mm, "end": v(127.05, 208.38) * mm});
            skLineSegment(sketch, "E86", {"start": v(14.05, 118.38) * mm, "end": v(174.05, 118.38) * mm, "construction": true});
            skLineSegment(sketch, "E87.0.MirrorCS", {"start": v(61.05, 28.38) * mm, "end": v(79.05, 10.38) * mm});
            skLineSegment(sketch, "E88.0.MirrorCS", {"start": v(79.05, 10.38) * mm, "end": v(79.05, -1.62) * mm});
            skArc(sketch, "E89.0.MirrorCS", {"start": v(79.05, -1.62) * mm, "mid": v(94.05, -16.62) * mm, "end": v(109.05, -1.62) * mm});
            skLineSegment(sketch, "E90.0.MirrorCS", {"start": v(109.05, -1.62) * mm, "end": v(109.05, 10.38) * mm});
            skLineSegment(sketch, "E91.0.MirrorCS", {"start": v(109.05, 10.38) * mm, "end": v(127.05, 28.38) * mm});
            skLineSegment(sketch, "E92.0.MirrorCS", {"start": v(94.05, 28.38) * mm, "end": v(94.05, -1.62) * mm, "construction": true});
            skLineSegment(sketch, "E93.0", {"start": v(174.05, 38.38) * mm, "end": v(174.05, 198.38) * mm});
            skArc(sketch, "E93.1", {"start": v(174.05, 198.38) * mm, "mid": v(171.12, 205.45) * mm, "end": v(164.05, 208.38) * mm});
            skCircle(sketch, "E94", {"center": v(94.05, 238.38) * mm, "radius": 6 * mm});
            skCircle(sketch, "E95.0.MirrorC", {"center": v(94.05, -1.62) * mm, "radius": 6 * mm});
            skSolve(sketch);
        }
        {
            var Q0;
            {var subQ1=sQuery(id+"F16.wireOp",EDGE,"E81");var subQ7=sQuery(id+"F16.wireOp",EDGE,"E87.0.MirrorCS");Q0=qUnion([makeQuery(id+"F16.imprint","IMPRINT",FACE,{"disambiguationData":[TD([[makeQuery(id+"F16.imprint","IMPRINT",EDGE,{"derivedFrom":subQ1}),-1.0]])]}),makeQuery(id+"F16.imprint","IMPRINT",FACE,{"disambiguationData":[TD([[makeQuery(id+"F16.imprint","IMPRINT",EDGE,{"derivedFrom":subQ7}),1.0]])]}),makeQuery(id+"F16.imprint","IMPRINT",FACE,{"disambiguationData":[TD([[makeQuery(id+"F16.imprint","IMPRINT",EDGE,{"derivedFrom":sQuery(id+"F16.wireOp",EDGE,"E79.0")}),-1.0]])]})]);}
            var Q1;
            Q1=makeQuery(id+"F2.opExtrude","CAP_FACE",FACE,{"disambiguationData":[OSD([sQuery(id+"F0.wireOp",EDGE,"E12"),sQuery(id+"F0.wireOp",EDGE,"E13"),sQuery(id+"F0.wireOp",EDGE,"E14"),sQuery(id+"F0.wireOp",EDGE,"E15"),sQuery(id+"F0.wireOp",EDGE,"E17.filletArc"),sQuery(id+"F0.wireOp",EDGE,"E18.filletArc"),sQuery(id+"F0.wireOp",EDGE,"E19.filletArc"),sQuery(id+"F0.wireOp",EDGE,"E20.filletArc"),sQuery(id+"F0.wireOp",EDGE,"E25.0"),sQuery(id+"F0.wireOp",EDGE,"E25.1"),sQuery(id+"F0.wireOp",EDGE,"E25.2"),sQuery(id+"F0.wireOp",EDGE,"E25.3"),sQuery(id+"F0.wireOp",EDGE,"E25.4"),sQuery(id+"F0.wireOp",EDGE,"E25.5"),sQuery(id+"F0.wireOp",EDGE,"E25.6"),sQuery(id+"F0.wireOp",EDGE,"E25.7")])],"isStart":false});
            extrude(context, id + "F17", {"entities" : qUnion([Q0]), "endBound" : BoundingType.UP_TO_SURFACE, "endBoundEntityFace" : qUnion([Q1]), "depth" : 25 * mm});
        }
    });
